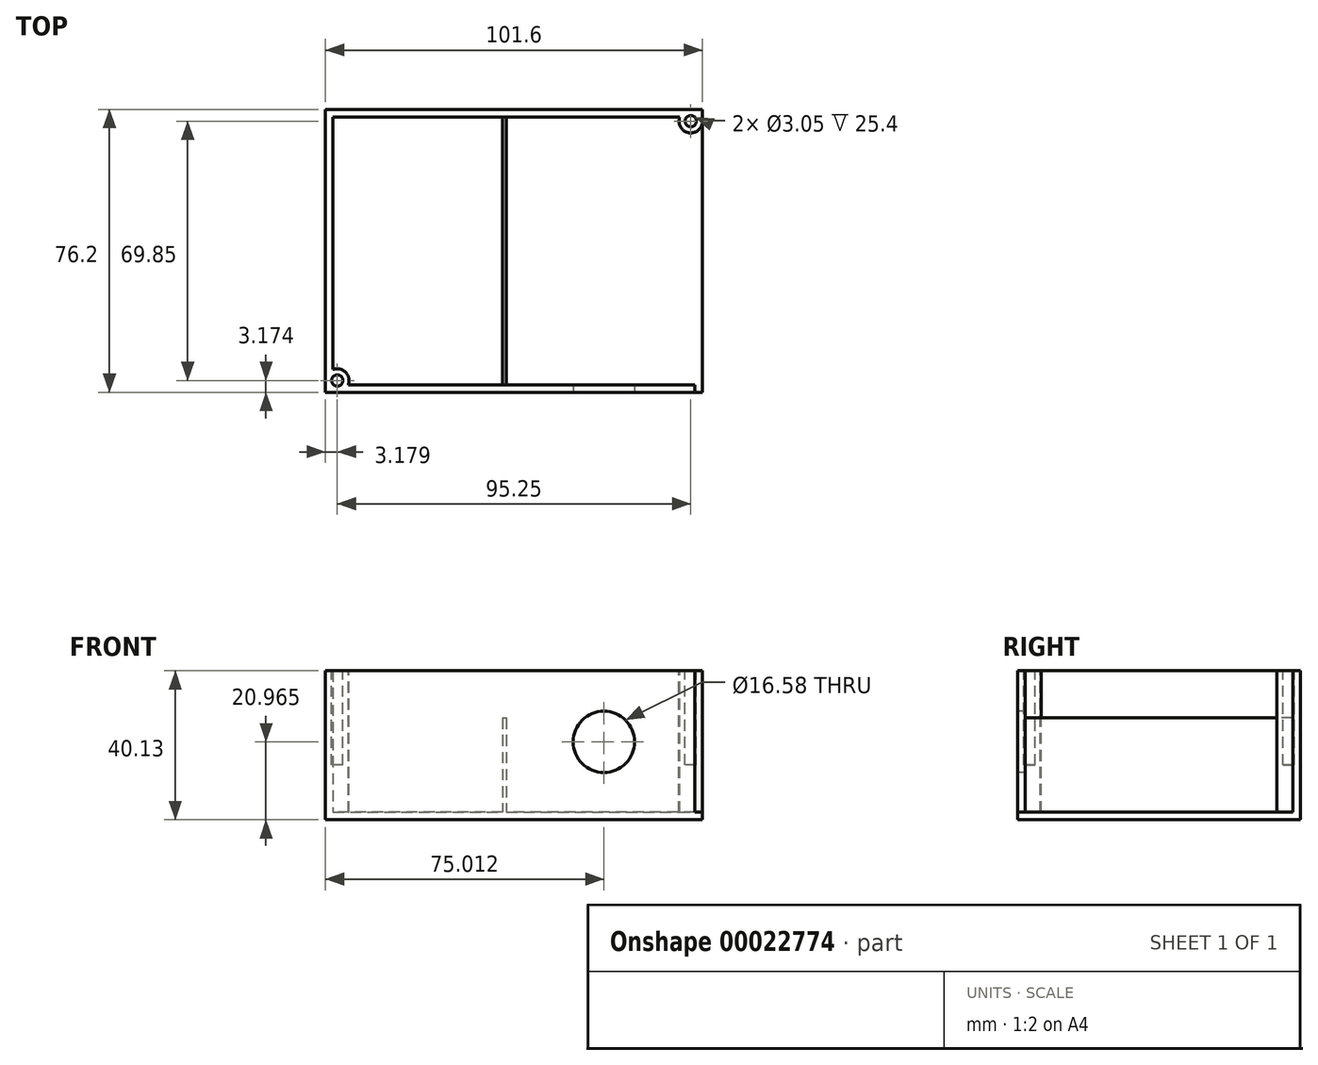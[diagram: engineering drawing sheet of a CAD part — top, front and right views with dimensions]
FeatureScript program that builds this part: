
annotation { "Feature Type Name" : "Feature", "Feature Type Description" : "" }
export const myFeature = defineFeature(function(context is Context, id is Id, definition is map)
    precondition{}
    {
        {
            var Q0;
            Q0=qCreatedBy(makeId("Top.planeOp"),FACE);
            var sketch = newSketch(context, id + "F0", { "sketchPlane" : qUnion([Q0])});
            skLineSegment(sketch, "E0.bottom", {"start": v(-48.77, -40.33) * mm, "end": v(52.83, -40.33) * mm});
            skLineSegment(sketch, "E0.top", {"start": v(-48.77, 35.87) * mm, "end": v(52.83, 35.87) * mm});
            skLineSegment(sketch, "E0.left", {"start": v(-48.77, -40.33) * mm, "end": v(-48.77, 35.87) * mm});
            skLineSegment(sketch, "E0.right", {"start": v(52.83, -40.33) * mm, "end": v(52.83, 35.87) * mm});
            skSolve(sketch);
        }
        {
            var Q0;
            Q0 = qSketchRegion(id + "F0", true);
            extrude(context, id + "F1", {"entities" : qUnion([Q0]), "depth" : 2.03 * mm});
        }
        {
            var Q0;
            Q0=makeQuery(id+"F1.opExtrude","CAP_FACE",FACE,{"disambiguationData":[OSD([sQuery(id+"F0.wireOp",EDGE,"E0.bottom"),sQuery(id+"F0.wireOp",EDGE,"E0.top"),sQuery(id+"F0.wireOp",EDGE,"E0.left"),sQuery(id+"F0.wireOp",EDGE,"E0.right")])],"isStart":false});
            var sketch = newSketch(context, id + "F2", { "sketchPlane" : qUnion([Q0])});
            skLineSegment(sketch, "E1.bottom", {"start": v(-48.77, 35.87) * mm, "end": v(-46.73, 35.87) * mm});
            skLineSegment(sketch, "E1.top", {"start": v(-48.77, -40.33) * mm, "end": v(-46.73, -40.33) * mm});
            skLineSegment(sketch, "E1.left", {"start": v(-48.77, 35.87) * mm, "end": v(-48.77, -40.33) * mm});
            skLineSegment(sketch, "E1.right", {"start": v(-46.73, 35.87) * mm, "end": v(-46.73, -40.33) * mm});
            skLineSegment(sketch, "E2.bottom", {"start": v(-46.73, 35.87) * mm, "end": v(52.83, 35.87) * mm});
            skLineSegment(sketch, "E2.top", {"start": v(-46.73, 33.84) * mm, "end": v(52.83, 33.84) * mm});
            skLineSegment(sketch, "E2.left", {"start": v(-46.73, 35.87) * mm, "end": v(-46.73, 33.84) * mm});
            skLineSegment(sketch, "E2.right", {"start": v(52.83, 35.87) * mm, "end": v(52.83, 33.84) * mm});
            skLineSegment(sketch, "E3.bottom", {"start": v(52.83, 33.84) * mm, "end": v(50.8, 33.84) * mm});
            skLineSegment(sketch, "E3.top", {"start": v(52.83, -40.33) * mm, "end": v(50.8, -40.33) * mm});
            skLineSegment(sketch, "E3.left", {"start": v(52.83, 33.84) * mm, "end": v(52.83, -40.33) * mm});
            skLineSegment(sketch, "E3.right", {"start": v(50.8, 33.84) * mm, "end": v(50.8, -40.33) * mm});
            skLineSegment(sketch, "E4.bottom", {"start": v(50.8, -40.33) * mm, "end": v(-46.73, -40.33) * mm});
            skLineSegment(sketch, "E4.top", {"start": v(50.8, -38.3) * mm, "end": v(-46.73, -38.3) * mm});
            skLineSegment(sketch, "E4.left", {"start": v(50.8, -40.33) * mm, "end": v(50.8, -38.3) * mm});
            skLineSegment(sketch, "E4.right", {"start": v(-46.73, -40.33) * mm, "end": v(-46.73, -38.3) * mm});
            skSolve(sketch);
        }
        {
            var Q0;
            Q0=makeQuery(id+"F2.imprint","IMPRINT",FACE,{"disambiguationData":[TD([[makeQuery(id+"F2.imprint","IMPRINT",EDGE,{"derivedFrom":sQuery(id+"F2.wireOp",EDGE,"E1.bottom")}),-1.0]])]});
            var Q1;
            Q1=makeQuery(id+"F2.imprint","IMPRINT",FACE,{"disambiguationData":[TD([[makeQuery(id+"F2.imprint","IMPRINT",EDGE,{"derivedFrom":sQuery(id+"F2.wireOp",EDGE,"E2.bottom")}),-1.0]])]});
            var Q2;
            Q2=makeQuery(id+"F2.imprint","IMPRINT",FACE,{"disambiguationData":[TD([[makeQuery(id+"F2.imprint","IMPRINT",EDGE,{"derivedFrom":sQuery(id+"F2.wireOp",EDGE,"E4.bottom")}),1.0]])]});
            var Q3;
            Q3=makeQuery(id+"F2.imprint","IMPRINT",FACE,{"disambiguationData":[TD([[makeQuery(id+"F2.imprint","IMPRINT",EDGE,{"derivedFrom":sQuery(id+"F2.wireOp",EDGE,"E3.bottom")}),1.0]])]});
            extrude(context, id + "F3", {"entities" : qUnion([Q0, Q1, Q2, Q3]), "operationType" : NewBodyOperationType.ADD, "depth" : 38.1 * mm});
        }
        {
            var Q0;
            Q0=makeQuery(id+"F1.opExtrude","CAP_FACE",FACE,{"disambiguationData":[OSD([sQuery(id+"F0.wireOp",EDGE,"E0.bottom"),sQuery(id+"F0.wireOp",EDGE,"E0.top"),sQuery(id+"F0.wireOp",EDGE,"E0.left"),sQuery(id+"F0.wireOp",EDGE,"E0.right")])],"isStart":false});
            var sketch = newSketch(context, id + "F4", { "sketchPlane" : qUnion([Q0])});
            skLineSegment(sketch, "E5.bottom", {"start": v(-1.02, 33.84) * mm, "end": v(0, 33.84) * mm});
            skLineSegment(sketch, "E5.top", {"start": v(-1.02, -38.3) * mm, "end": v(0, -38.3) * mm});
            skLineSegment(sketch, "E5.left", {"start": v(-1.02, 33.84) * mm, "end": v(-1.02, -38.3) * mm});
            skLineSegment(sketch, "E5.right", {"start": v(0, 33.84) * mm, "end": v(0, -38.3) * mm});
            skSolve(sketch);
        }
        {
            var Q0;
            Q0=makeQuery(id+"F4.imprint","IMPRINT",FACE,{"disambiguationData":[TD([[makeQuery(id+"F4.imprint","IMPRINT",EDGE,{"derivedFrom":sQuery(id+"F4.wireOp",EDGE,"E5.bottom")}),-1.0]])]});
            extrude(context, id + "F5", {"entities" : qUnion([Q0]), "operationType" : NewBodyOperationType.ADD, "depth" : 25.4 * mm});
        }
        {
            var Q0;
            Q0=makeQuery(id+"F3.boolean.opBoolean","MERGE",FACE,{"derivedFrom":[makeQuery(id+"F1.opExtrude","SWEPT_FACE",FACE,{"disambiguationData":[OSD([sQuery(id+"F0.wireOp",EDGE,"E0.bottom")])]}),makeQuery(id+"F3.opExtrude","SWEPT_FACE",FACE,{"disambiguationData":[OSD([sQuery(id+"F2.wireOp",EDGE,"E1.top"),sQuery(id+"F2.wireOp",EDGE,"E3.top"),sQuery(id+"F2.wireOp",EDGE,"E4.bottom")])]})]});
            var sketch = newSketch(context, id + "F6", { "sketchPlane" : qUnion([Q0])});
            skCircle(sketch, "E6", {"center": v(26.24, 20.97) * mm, "radius": 8.3 * mm});
            skSolve(sketch);
        }
        {
            var Q0;
            Q0=makeQuery(id+"F6.imprint","IMPRINT",FACE,{"disambiguationData":[TD([[makeQuery(id+"F6.imprint","IMPRINT",EDGE,{"derivedFrom":sQuery(id+"F6.wireOp",EDGE,"E6")}),1.0]])]});
            extrude(context, id + "F7", {"entities" : qUnion([Q0]), "operationType" : NewBodyOperationType.REMOVE, "endBound" : BoundingType.UP_TO_NEXT, "oppositeDirection" : true, "depth" : 25.4 * mm});
        }
        {
            var Q0;
            Q0=makeQuery(id+"F3.opExtrude","CAP_FACE",FACE,{"disambiguationData":[OSD([sQuery(id+"F2.wireOp",EDGE,"E1.bottom"),sQuery(id+"F2.wireOp",EDGE,"E1.top"),sQuery(id+"F2.wireOp",EDGE,"E1.left"),sQuery(id+"F2.wireOp",EDGE,"E1.right"),sQuery(id+"F2.wireOp",EDGE,"E2.bottom"),sQuery(id+"F2.wireOp",EDGE,"E2.top"),sQuery(id+"F2.wireOp",EDGE,"E2.right"),sQuery(id+"F2.wireOp",EDGE,"E3.top"),sQuery(id+"F2.wireOp",EDGE,"E3.left"),sQuery(id+"F2.wireOp",EDGE,"E3.right"),sQuery(id+"F2.wireOp",EDGE,"E4.bottom"),sQuery(id+"F2.wireOp",EDGE,"E4.top")])],"isStart":false});
            var sketch = newSketch(context, id + "F8", { "sketchPlane" : qUnion([Q0])});
            skCircle(sketch, "E7", {"center": v(49.66, 32.7) * mm, "radius": 3.18 * mm});
            skCircle(sketch, "E8", {"center": v(-45.6, -37.16) * mm, "radius": 3.18 * mm});
            skSolve(sketch);
        }
        {
            var Q0;
            {var subQ1=sQuery(id+"F8.wireOp",EDGE,"E8");var subQ3=makeQuery(id+"F3.opExtrude","CAP_EDGE",EDGE,{"disambiguationData":[OSD([sQuery(id+"F2.wireOp",EDGE,"E1.right")])],"isStart":false});var subQ5=makeQuery(id+"F8.imprint","INTERSECT",VERTEX,{"derivedFrom":[subQ3,subQ1]});Q0=makeQuery(id+"F8.imprint","IMPRINT",FACE,{"disambiguationData":[TD([[makeQuery(id+"F8.imprint","IMPRINT",EDGE,{"disambiguationData":[TD([[subQ5,1.0]])],"derivedFrom":subQ1}),1.0]])]});}
            var Q1;
            {var subQ1=sQuery(id+"F8.wireOp",EDGE,"E7");var subQ3=makeQuery(id+"F3.opExtrude","CAP_EDGE",EDGE,{"disambiguationData":[OSD([sQuery(id+"F2.wireOp",EDGE,"E2.top")])],"isStart":false});var subQ5=makeQuery(id+"F8.imprint","INTERSECT",VERTEX,{"derivedFrom":[subQ3,subQ1]});Q1=makeQuery(id+"F8.imprint","IMPRINT",FACE,{"disambiguationData":[TD([[makeQuery(id+"F8.imprint","IMPRINT",EDGE,{"disambiguationData":[TD([[subQ5,-1.0]])],"derivedFrom":subQ1}),1.0]])]});}
            extrude(context, id + "F9", {"entities" : qUnion([Q0, Q1]), "operationType" : NewBodyOperationType.ADD, "oppositeDirection" : true, "depth" : 38.1 * mm});
        }
        {
            var Q0;
            {var subQ0=sQuery(id+"F2.wireOp",EDGE,"E1.right");var subQ1=sQuery(id+"F2.wireOp",EDGE,"E2.top");var subQ2=sQuery(id+"F2.wireOp",EDGE,"E3.right");var subQ3=sQuery(id+"F2.wireOp",EDGE,"E4.top");Q0=makeQuery(id+"F9.boolean.opBoolean","MERGE",FACE,{"derivedFrom":[makeQuery(id+"F3.opExtrude","CAP_FACE",FACE,{"disambiguationData":[OSD([sQuery(id+"F2.wireOp",EDGE,"E1.bottom"),sQuery(id+"F2.wireOp",EDGE,"E1.top"),sQuery(id+"F2.wireOp",EDGE,"E1.left"),subQ0,sQuery(id+"F2.wireOp",EDGE,"E2.bottom"),subQ1,sQuery(id+"F2.wireOp",EDGE,"E2.right"),sQuery(id+"F2.wireOp",EDGE,"E3.top"),sQuery(id+"F2.wireOp",EDGE,"E3.left"),subQ2,sQuery(id+"F2.wireOp",EDGE,"E4.bottom"),subQ3])],"isStart":false}),makeQuery(id+"F9.opExtrude","CAP_FACE",FACE,{"disambiguationData":[OSD([subQ1,subQ2,sQuery(id+"F8.wireOp",EDGE,"E7")])],"isStart":true}),makeQuery(id+"F9.opExtrude","CAP_FACE",FACE,{"disambiguationData":[OSD([subQ0,subQ3,sQuery(id+"F8.wireOp",EDGE,"E8")])],"isStart":true})]});}
            var sketch = newSketch(context, id + "F10", { "sketchPlane" : qUnion([Q0])});
            skCircle(sketch, "E9", {"center": v(49.66, 32.7) * mm, "radius": 1.52 * mm});
            skCircle(sketch, "E10", {"center": v(-45.6, -37.16) * mm, "radius": 1.52 * mm});
            skSolve(sketch);
        }
        {
            var Q0;
            Q0=makeQuery(id+"F10.imprint","IMPRINT",FACE,{"disambiguationData":[TD([[makeQuery(id+"F10.imprint","IMPRINT",EDGE,{"derivedFrom":sQuery(id+"F10.wireOp",EDGE,"E10")}),1.0]])]});
            var Q1;
            Q1=makeQuery(id+"F10.imprint","IMPRINT",FACE,{"disambiguationData":[TD([[makeQuery(id+"F10.imprint","IMPRINT",EDGE,{"derivedFrom":sQuery(id+"F10.wireOp",EDGE,"E9")}),1.0]])]});
            extrude(context, id + "F11", {"entities" : qUnion([Q0, Q1]), "operationType" : NewBodyOperationType.REMOVE, "oppositeDirection" : true, "depth" : 25.4 * mm});
        }
    });
